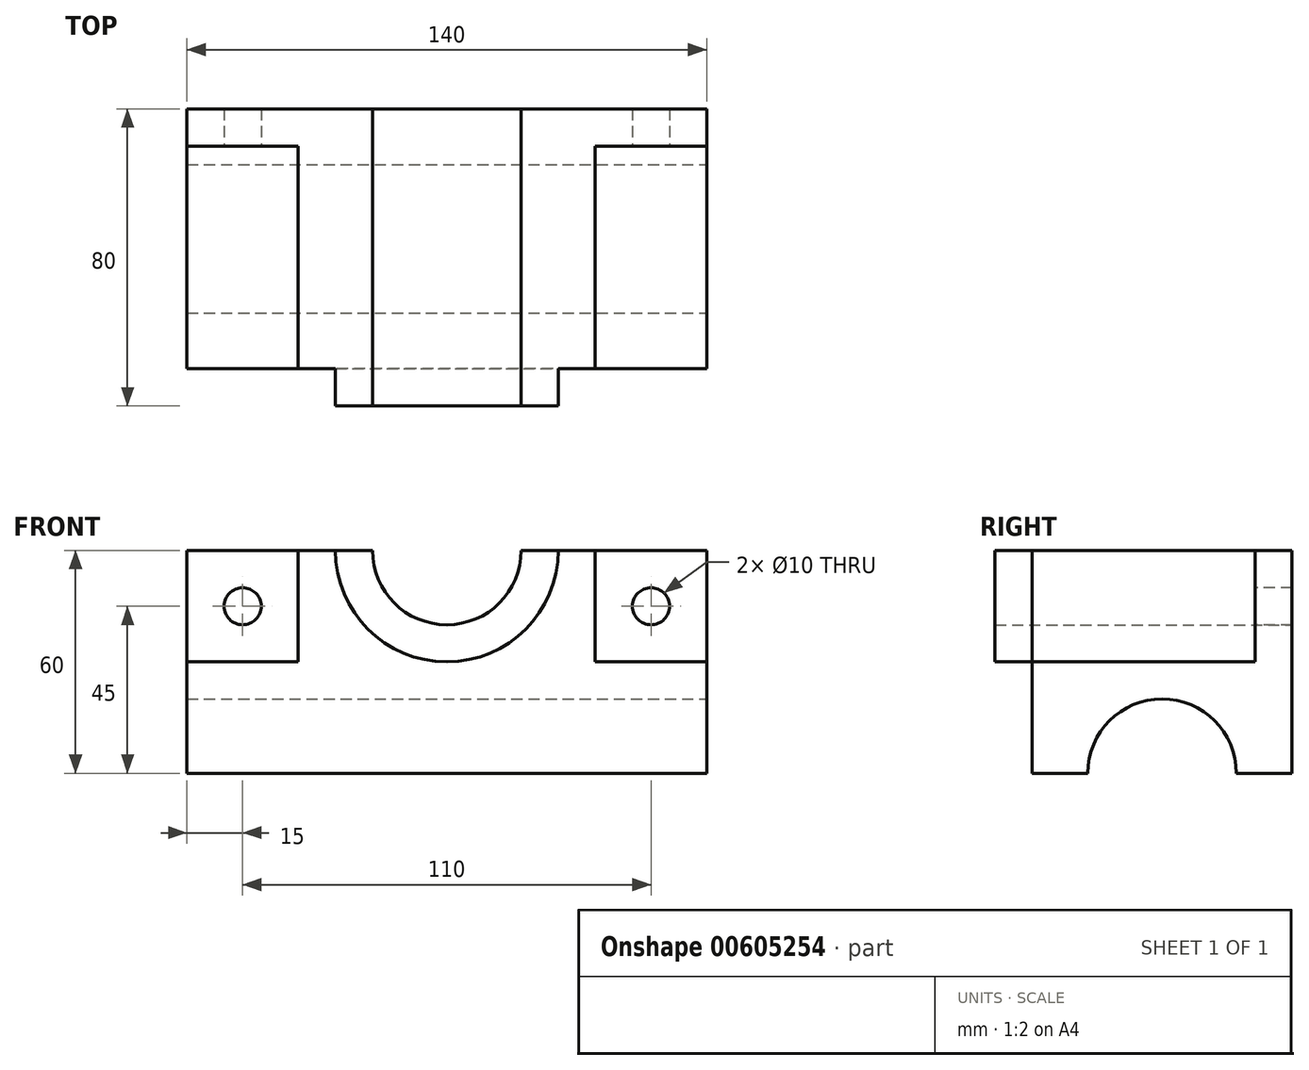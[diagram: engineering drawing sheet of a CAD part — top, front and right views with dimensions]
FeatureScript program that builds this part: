
annotation { "Feature Type Name" : "Feature", "Feature Type Description" : "" }
export const myFeature = defineFeature(function(context is Context, id is Id, definition is map)
    precondition{}
    {
        {
            var Q0;
            Q0=qCreatedBy(makeId("Top.planeOp"),FACE);
            var sketch = newSketch(context, id + "F0", { "sketchPlane" : qUnion([Q0])});
            skLineSegment(sketch, "E0.bottom", {"start": v(70, 35) * mm, "end": v(-70, 35) * mm});
            skLineSegment(sketch, "E0.top", {"start": v(70, -35) * mm, "end": v(-70, -35) * mm});
            skLineSegment(sketch, "E0.left", {"start": v(70, 35) * mm, "end": v(70, -35) * mm});
            skLineSegment(sketch, "E0.right", {"start": v(-70, 35) * mm, "end": v(-70, -35) * mm});
            skPoint(sketch, "E0.middle", {"position": v(0, 0) * mm});
            skSolve(sketch);
        }
        {
            var Q0;
            Q0=makeQuery(id+"F0.imprint","IMPRINT",FACE,{"disambiguationData":[TD([[makeQuery(id+"F0.imprint","IMPRINT",EDGE,{"derivedFrom":sQuery(id+"F0.wireOp",EDGE,"E0.bottom")}),1.0]])]});
            extrude(context, id + "F1", {"entities" : qUnion([Q0]), "depth" : 60 * mm, "offsetDistance" : 25 * mm});
        }
        {
            var Q0;
            Q0=makeQuery(id+"F1.opExtrude","SWEPT_FACE",FACE,{"disambiguationData":[OSD([sQuery(id+"F0.wireOp",EDGE,"E0.left")])]});
            var sketch = newSketch(context, id + "F2", { "sketchPlane" : qUnion([Q0])});
            skCircle(sketch, "E1", {"center": v(0, 0) * mm, "radius": 20 * mm});
            skSolve(sketch);
        }
        {
            var Q0;
            {var subQ0=sQuery(id+"F2.wireOp",EDGE,"E1");var subQ1=makeQuery(id+"F1.opExtrude","CAP_EDGE",EDGE,{"disambiguationData":[OSD([sQuery(id+"F0.wireOp",EDGE,"E0.left")])],"isStart":true});var subQ2=makeQuery(id+"F2.imprint","INTERSECT",VERTEX,{"disambiguationData":[OD(0.0)],"derivedFrom":[subQ1,subQ0]});Q0=makeQuery(id+"F2.imprint","IMPRINT",FACE,{"disambiguationData":[TD([[makeQuery(id+"F2.imprint","IMPRINT",EDGE,{"disambiguationData":[TD([[subQ2,-1.0]])],"derivedFrom":subQ0}),1.0]])]});}
            extrude(context, id + "F3", {"entities" : qUnion([Q0]), "operationType" : NewBodyOperationType.REMOVE, "endBound" : BoundingType.THROUGH_ALL, "oppositeDirection" : true, "depth" : 25 * mm, "offsetDistance" : 25 * mm});
        }
        {
            var Q0;
            Q0=makeQuery(id+"F1.opExtrude","CAP_FACE",FACE,{"disambiguationData":[OSD([sQuery(id+"F0.wireOp",EDGE,"E0.bottom"),sQuery(id+"F0.wireOp",EDGE,"E0.top"),sQuery(id+"F0.wireOp",EDGE,"E0.left"),sQuery(id+"F0.wireOp",EDGE,"E0.right")])],"isStart":false});
            var sketch = newSketch(context, id + "F4", { "sketchPlane" : qUnion([Q0])});
            skLineSegment(sketch, "E2.bottom", {"start": v(70, -35) * mm, "end": v(40, -35) * mm});
            skLineSegment(sketch, "E2.top", {"start": v(70, 25) * mm, "end": v(40, 25) * mm});
            skLineSegment(sketch, "E2.left", {"start": v(70, -35) * mm, "end": v(70, 25) * mm});
            skLineSegment(sketch, "E2.right", {"start": v(40, -35) * mm, "end": v(40, 25) * mm});
            skSolve(sketch);
        }
        {
            var Q0;
            Q0 = qSketchRegion(id + "F4", true);
            extrude(context, id + "F5", {"entities" : qUnion([Q0]), "operationType" : NewBodyOperationType.REMOVE, "oppositeDirection" : true, "depth" : 30 * mm, "offsetDistance" : 25 * mm});
        }
        {
            var Q0;
            Q0=makeQuery(id+"F5.boolean.opBoolean","COPY",FACE,{"derivedFrom":makeQuery(id+"F5.opExtrude","SWEPT_FACE",FACE,{"disambiguationData":[OSD([sQuery(id+"F4.wireOp",EDGE,"E2.top")])]})});
            var sketch = newSketch(context, id + "F6", { "sketchPlane" : qUnion([Q0])});
            skCircle(sketch, "E3", {"center": v(55, 45) * mm, "radius": 5 * mm});
            skSolve(sketch);
        }
        {
            var Q0;
            Q0=makeQuery(id+"F6.imprint","IMPRINT",FACE,{"disambiguationData":[TD([[makeQuery(id+"F6.imprint","IMPRINT",EDGE,{"derivedFrom":sQuery(id+"F6.wireOp",EDGE,"E3")}),1.0]])]});
            extrude(context, id + "F7", {"entities" : qUnion([Q0]), "operationType" : NewBodyOperationType.REMOVE, "endBound" : BoundingType.THROUGH_ALL, "oppositeDirection" : true, "depth" : 25 * mm, "offsetDistance" : 25 * mm});
        }
        {
            var Q0;
            Q0=makeQuery(id+"F1.opExtrude","CAP_FACE",FACE,{"disambiguationData":[OSD([sQuery(id+"F0.wireOp",EDGE,"E0.bottom"),sQuery(id+"F0.wireOp",EDGE,"E0.top"),sQuery(id+"F0.wireOp",EDGE,"E0.left"),sQuery(id+"F0.wireOp",EDGE,"E0.right")])],"isStart":false});
            var sketch = newSketch(context, id + "F8", { "sketchPlane" : qUnion([Q0])});
            skLineSegment(sketch, "E4.bottom", {"start": v(-70, -35) * mm, "end": v(-40, -35) * mm});
            skLineSegment(sketch, "E4.top", {"start": v(-70, 25) * mm, "end": v(-40, 25) * mm});
            skLineSegment(sketch, "E4.left", {"start": v(-70, -35) * mm, "end": v(-70, 25) * mm});
            skLineSegment(sketch, "E4.right", {"start": v(-40, -35) * mm, "end": v(-40, 25) * mm});
            skSolve(sketch);
        }
        {
            var Q0;
            Q0=makeQuery(id+"F8.imprint","IMPRINT",FACE,{"disambiguationData":[TD([[makeQuery(id+"F8.imprint","IMPRINT",EDGE,{"derivedFrom":sQuery(id+"F8.wireOp",EDGE,"E4.bottom")}),-1.0]])]});
            extrude(context, id + "F9", {"entities" : qUnion([Q0]), "operationType" : NewBodyOperationType.REMOVE, "oppositeDirection" : true, "depth" : 30 * mm, "offsetDistance" : 25 * mm});
        }
        {
            var Q0;
            Q0=makeQuery(id+"F9.boolean.opBoolean","COPY",FACE,{"derivedFrom":makeQuery(id+"F9.opExtrude","SWEPT_FACE",FACE,{"disambiguationData":[OSD([sQuery(id+"F8.wireOp",EDGE,"E4.top")])]})});
            var sketch = newSketch(context, id + "F10", { "sketchPlane" : qUnion([Q0])});
            skCircle(sketch, "E5", {"center": v(-55, 45) * mm, "radius": 5 * mm});
            skSolve(sketch);
        }
        {
            var Q0;
            Q0=makeQuery(id+"F10.imprint","IMPRINT",FACE,{"disambiguationData":[TD([[makeQuery(id+"F10.imprint","IMPRINT",EDGE,{"derivedFrom":sQuery(id+"F10.wireOp",EDGE,"E5")}),1.0]])]});
            extrude(context, id + "F11", {"entities" : qUnion([Q0]), "operationType" : NewBodyOperationType.REMOVE, "endBound" : BoundingType.THROUGH_ALL, "oppositeDirection" : true, "depth" : 25 * mm, "offsetDistance" : 25 * mm});
        }
        {
            var Q0;
            Q0=makeQuery(id+"F1.opExtrude","SWEPT_FACE",FACE,{"disambiguationData":[OSD([sQuery(id+"F0.wireOp",EDGE,"E0.top")])]});
            var sketch = newSketch(context, id + "F12", { "sketchPlane" : qUnion([Q0])});
            skCircle(sketch, "E6", {"center": v(0, 60) * mm, "radius": 30 * mm});
            skCircle(sketch, "E7", {"center": v(0, 60) * mm, "radius": 20 * mm});
            skSolve(sketch);
        }
        {
            var Q0;
            {var subQ0=sQuery(id+"F12.wireOp",EDGE,"E6");var subQ1=makeQuery(id+"F1.opExtrude","CAP_EDGE",EDGE,{"disambiguationData":[OSD([sQuery(id+"F0.wireOp",EDGE,"E0.top")])],"isStart":false});var subQ2=makeQuery(id+"F12.imprint","INTERSECT",VERTEX,{"disambiguationData":[OD(0.0)],"derivedFrom":[subQ1,subQ0]});Q0=makeQuery(id+"F12.imprint","IMPRINT",FACE,{"disambiguationData":[TD([[makeQuery(id+"F12.imprint","IMPRINT",EDGE,{"disambiguationData":[TD([[subQ2,1.0]])],"derivedFrom":subQ0}),1.0]])]});}
            extrude(context, id + "F13", {"entities" : qUnion([Q0]), "operationType" : NewBodyOperationType.ADD, "depth" : 10 * mm, "offsetDistance" : 25 * mm});
        }
        {
            var Q0;
            {var subQ0=sQuery(id+"F0.wireOp",EDGE,"E0.top");var subQ3=sQuery(id+"F12.wireOp",EDGE,"E7");Q0=makeQuery(id+"F13.boolean.opBoolean","SPLIT",FACE,{"disambiguationData":[TD([makeQuery(id+"F13.opExtrude","SWEPT_FACE",FACE,{"disambiguationData":[OSD([subQ3])]})])],"derivedFrom":makeQuery(id+"F1.opExtrude","SWEPT_FACE",FACE,{"disambiguationData":[OSD([subQ0])]})});}
            extrude(context, id + "F14", {"entities" : qUnion([Q0]), "operationType" : NewBodyOperationType.REMOVE, "endBound" : BoundingType.THROUGH_ALL, "oppositeDirection" : true, "depth" : 25 * mm, "offsetDistance" : 25 * mm});
        }
    });
